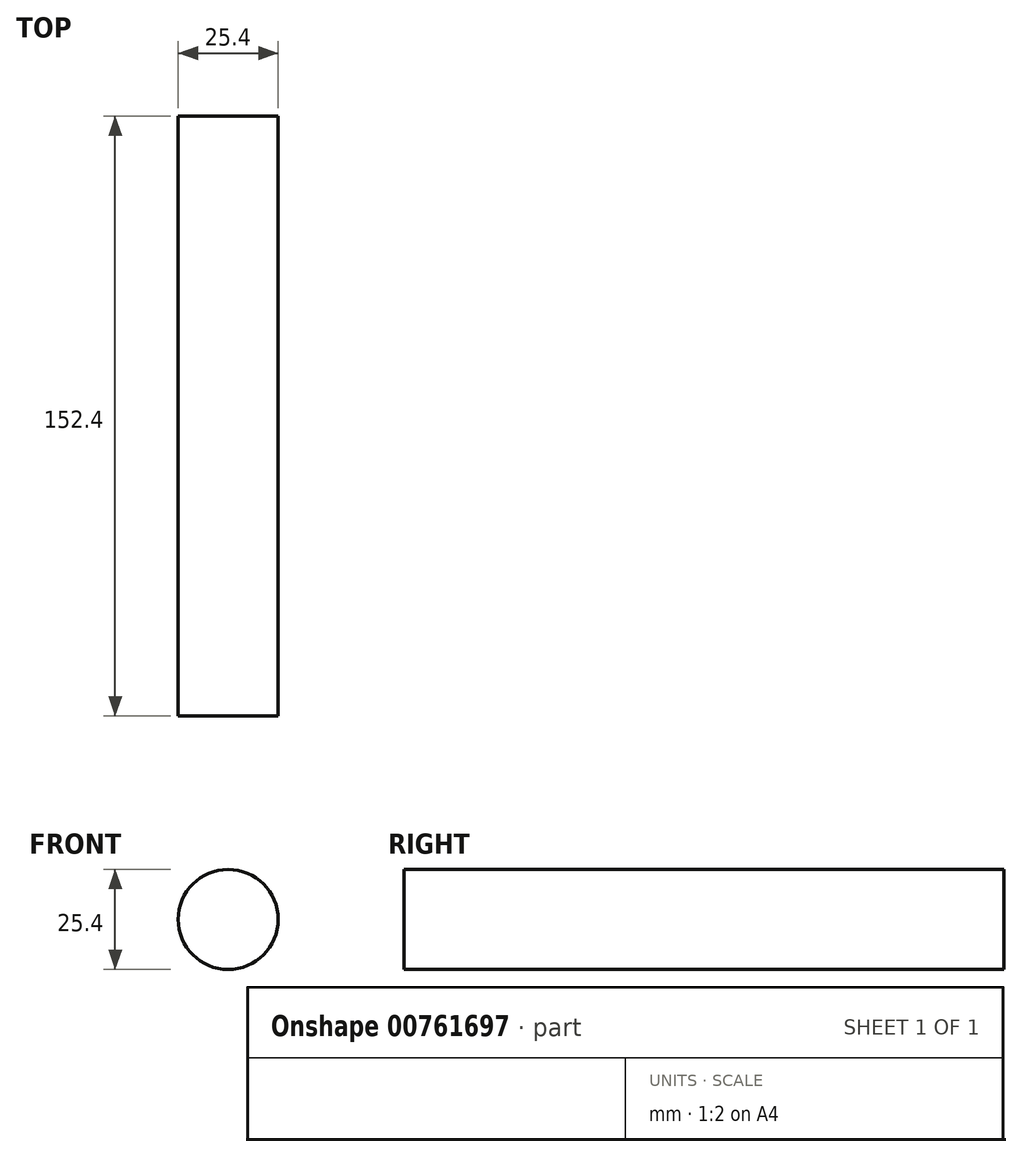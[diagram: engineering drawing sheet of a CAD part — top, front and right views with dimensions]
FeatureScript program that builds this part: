
annotation { "Feature Type Name" : "Feature", "Feature Type Description" : "" }
export const myFeature = defineFeature(function(context is Context, id is Id, definition is map)
    precondition{}
    {
        {
            var Q0;
            Q0=qCreatedBy(makeId("Front.planeOp"),FACE);
            var sketch = newSketch(context, id + "F0", { "sketchPlane" : qUnion([Q0])});
            skCircle(sketch, "E0", {"center": v(0, 0) * mm, "radius": 12.7 * mm});
            skSolve(sketch);
        }
        {
            var Q0;
            Q0 = qSketchRegion(id + "F0", true);
            extrude(context, id + "F1", {"entities" : qUnion([Q0]), "depth" : 152.4 * mm, "offsetDistance" : 25.4 * mm});
        }
    });
